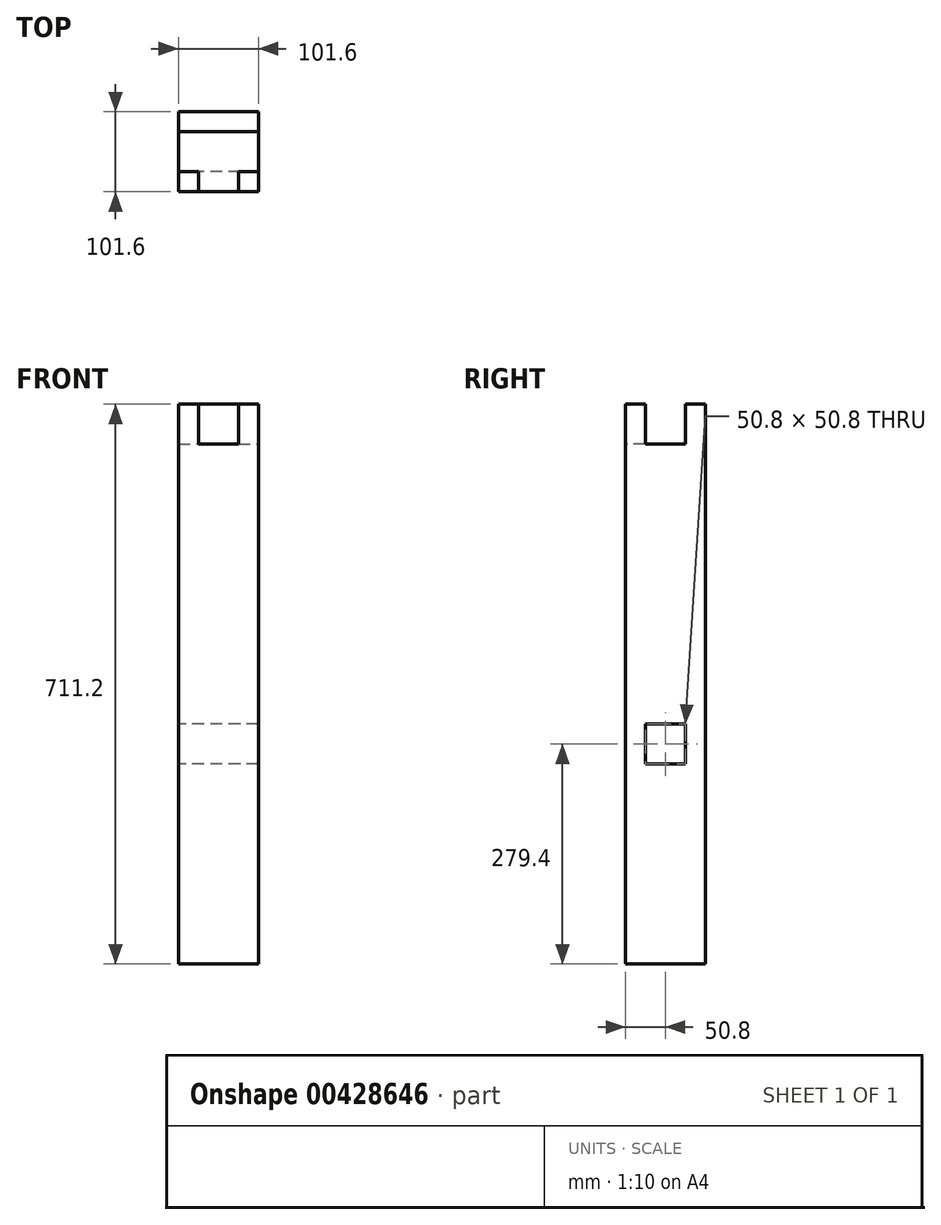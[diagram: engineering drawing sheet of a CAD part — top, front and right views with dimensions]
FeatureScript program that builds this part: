
annotation { "Feature Type Name" : "Feature", "Feature Type Description" : "" }
export const myFeature = defineFeature(function(context is Context, id is Id, definition is map)
    precondition{}
    {
        {
            var Q0;
            Q0=qCreatedBy(makeId("Front.planeOp"),FACE);
            var sketch = newSketch(context, id + "F0", { "sketchPlane" : qUnion([Q0])});
            skLineSegment(sketch, "E0.bottom", {"start": v(-50.8, 355.6) * mm, "end": v(50.8, 355.6) * mm});
            skLineSegment(sketch, "E0.top", {"start": v(-50.8, -355.6) * mm, "end": v(50.8, -355.6) * mm});
            skLineSegment(sketch, "E0.left", {"start": v(-50.8, 355.6) * mm, "end": v(-50.8, -355.6) * mm});
            skLineSegment(sketch, "E0.right", {"start": v(50.8, 355.6) * mm, "end": v(50.8, -355.6) * mm});
            skPoint(sketch, "E0.middle", {"position": v(0, 0) * mm});
            skSolve(sketch);
        }
        {
            var Q0;
            Q0=makeQuery(id+"F0.imprint","IMPRINT",FACE,{"disambiguationData":[TD([[makeQuery(id+"F0.imprint","IMPRINT",EDGE,{"derivedFrom":sQuery(id+"F0.wireOp",EDGE,"E0.bottom")}),-1.0]])]});
            extrude(context, id + "F1", {"entities" : qUnion([Q0]), "depth" : 101.6 * mm});
        }
        {
            var Q0;
            Q0=makeQuery(id+"F1.opExtrude","CAP_FACE",FACE,{"disambiguationData":[OSD([sQuery(id+"F0.wireOp",EDGE,"E0.bottom"),sQuery(id+"F0.wireOp",EDGE,"E0.top"),sQuery(id+"F0.wireOp",EDGE,"E0.left"),sQuery(id+"F0.wireOp",EDGE,"E0.right")])],"isStart":false});
            var sketch = newSketch(context, id + "F2", { "sketchPlane" : qUnion([Q0])});
            skPoint(sketch, "E1.endSnap0", {"position": v(0, 355.6) * mm});
            skLineSegment(sketch, "E2.bottom", {"start": v(-25.4, 355.6) * mm, "end": v(25.4, 355.6) * mm});
            skLineSegment(sketch, "E2.top", {"start": v(-25.4, 304.8) * mm, "end": v(25.4, 304.8) * mm});
            skLineSegment(sketch, "E2.left", {"start": v(-25.4, 355.6) * mm, "end": v(-25.4, 304.8) * mm});
            skLineSegment(sketch, "E2.right", {"start": v(25.4, 355.6) * mm, "end": v(25.4, 304.8) * mm});
            skPoint(sketch, "E2.middle", {"position": v(0, 330.2) * mm});
            skSolve(sketch);
        }
        {
            var Q0;
            Q0=makeQuery(id+"F1.opExtrude","SWEPT_FACE",FACE,{"disambiguationData":[OSD([sQuery(id+"F0.wireOp",EDGE,"E0.right")])]});
            var sketch = newSketch(context, id + "F3", { "sketchPlane" : qUnion([Q0])});
            skPoint(sketch, "E3.endSnap0", {"position": v(-50.8, 355.6) * mm});
            skLineSegment(sketch, "E4.bottom", {"start": v(-76.2, 355.6) * mm, "end": v(-25.4, 355.6) * mm});
            skLineSegment(sketch, "E4.top", {"start": v(-76.2, 304.8) * mm, "end": v(-25.4, 304.8) * mm});
            skLineSegment(sketch, "E4.left", {"start": v(-76.2, 355.6) * mm, "end": v(-76.2, 304.8) * mm});
            skLineSegment(sketch, "E4.right", {"start": v(-25.4, 355.6) * mm, "end": v(-25.4, 304.8) * mm});
            skPoint(sketch, "E4.middle", {"position": v(-50.8, 330.2) * mm});
            skSolve(sketch);
        }
        {
            var Q0;
            Q0 = qSketchRegion(id + "F3", true);
            extrude(context, id + "F4", {"entities" : qUnion([Q0]), "operationType" : NewBodyOperationType.REMOVE, "oppositeDirection" : true, "depth" : 101.6 * mm});
        }
        {
            var Q0;
            Q0 = qSketchRegion(id + "F2", true);
            extrude(context, id + "F5", {"entities" : qUnion([Q0]), "operationType" : NewBodyOperationType.REMOVE, "oppositeDirection" : true, "depth" : 25.4 * mm});
        }
        {
            var Q0;
            Q0=makeQuery(id+"F1.opExtrude","SWEPT_FACE",FACE,{"disambiguationData":[OSD([sQuery(id+"F0.wireOp",EDGE,"E0.left")])]});
            var sketch = newSketch(context, id + "F6", { "sketchPlane" : qUnion([Q0])});
            skPoint(sketch, "E5.middle.positionSnap0", {"position": v(50.8, -355.6) * mm});
            skPoint(sketch, "E5.centerSnap0", {"position": v(50.8, -355.6) * mm});
            skLineSegment(sketch, "E6", {"start": v(50.8, -355.6) * mm, "end": v(50.8, -101.6) * mm});
            skLineSegment(sketch, "E7.bottom", {"start": v(76.2, -101.6) * mm, "end": v(25.4, -101.6) * mm});
            skLineSegment(sketch, "E7.top", {"start": v(76.2, -50.8) * mm, "end": v(25.4, -50.8) * mm});
            skLineSegment(sketch, "E7.left", {"start": v(76.2, -101.6) * mm, "end": v(76.2, -50.8) * mm});
            skLineSegment(sketch, "E7.right", {"start": v(25.4, -101.6) * mm, "end": v(25.4, -50.8) * mm});
            skSolve(sketch);
        }
        {
            var Q0;
            Q0 = qSketchRegion(id + "F6", true);
            extrude(context, id + "F7", {"entities" : qUnion([Q0]), "operationType" : NewBodyOperationType.REMOVE, "oppositeDirection" : true, "depth" : 101.6 * mm});
        }
    });
